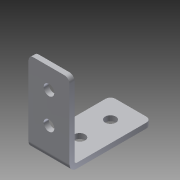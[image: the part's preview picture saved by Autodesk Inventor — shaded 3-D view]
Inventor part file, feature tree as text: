
AUTODESK INVENTOR PART (.ipt)
format: ipt  version: 2014 SP1 (Build 180222100, 222)  size: 185,856 bytes
history: native  units: in
note: dims shown in document units (in); Inventor stores cm internally (conversion verified against a paired STEP export)
features: other x4, sheet_metal_op x3, sketch x3, chamfer x1
ambient origin geometry x8: Origin, YZ Plane, XZ Plane, XY Plane, X Axis, Y Axis, Z Axis, Center Point
bodies: Solid1 (feature_tree)
feature tree (11):
  sheet_metal_op  "Face1"
  sheet_metal_op  "Flange1"
  chamfer  "Corner Round1"
  sketch  "Sketch1"  dims[d0=0.26in]
  other  "Plate1"
  sketch  "Sketch2"  dims[d2=1.0in]
  other  "Plate2"
  sheet_metal_op  "Bend1"
  sketch  "Sketch3"  dims[d3=2.0in d4=0.75in d5=0.75in d6=0.125in d7=0.125in d8=0.0625in d9=0.25in d10=0.125in d11=2.0in d12=90.0deg d13=0.05in d14=0.5in d15=0.125in d16=0.125in d17=0.75in d18=0.75in d19=0.26in d20=0.125in d21=0.0in d22=0.125in]
  other  "Cut1"
  other  "Definition1"
